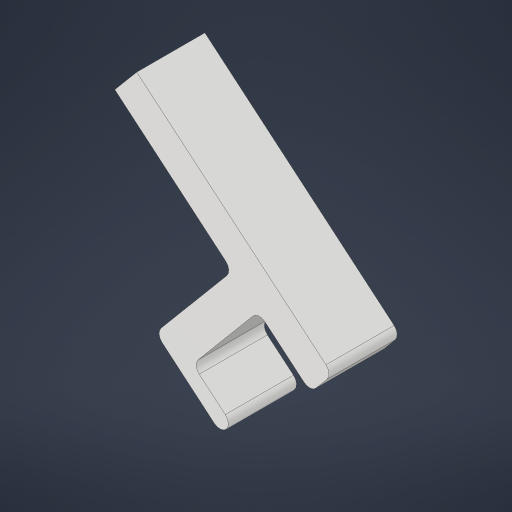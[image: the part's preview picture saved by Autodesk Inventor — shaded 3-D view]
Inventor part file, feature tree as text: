
AUTODESK INVENTOR PART (.ipt)
format: ipt  version: 2023.4 (Build 274418000, 418)  size: 199,168 bytes
history: native  units: in
note: dims shown in document units (in); Inventor stores cm internally (conversion verified against a paired STEP export)
features: extrude x1, fillet x1, sketch x1
ambient origin geometry x8: Origin, YZ Plane, XZ Plane, XY Plane, X Axis, Y Axis, Z Axis, Center Point
bodies: Solid1 (feature_tree)
feature tree (3):
  extrude  "Extrusion1"  Depth=0.125in
  fillet  "Fillet1"  Radius=1.813in
  sketch  "Sketch1"  dims[d0=5.0in d1=3.0in d2=1.813in d3=7.315in d4=0.75in d5=1.25in d6=0.5in d7=0.5in d8=1.0in d9=1.75in d11=0.75in d13=0.25in d14=0.3436in d15=3.75in d16=1.0in d17=0.0in d18=0.125in]
